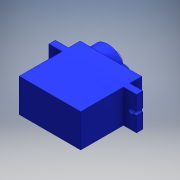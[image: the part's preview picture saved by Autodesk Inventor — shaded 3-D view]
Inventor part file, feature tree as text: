
AUTODESK INVENTOR PART (.ipt)
format: ipt  version: 2016 (Build 200138000, 138)  size: 201,216 bytes
history: native  units: mm
features: extrude x8, sketch x8
ambient origin geometry x8: Origin, YZ Plane, XZ Plane, XY Plane, X Axis, Y Axis, Z Axis, Center Point
bodies: Solid1 (feature_tree)
feature tree (16):
  extrude  "Extrusion1"  TaperAngle=0.0deg  [1 undecoded]
  extrude  "Extrusion2"  Depth=2.38mm
  extrude  "Extrusion3"  Depth=4.82mm
  extrude  "Extrusion4"  TaperAngle=0.0deg  [1 undecoded]
  extrude  "Extrusion5"  Depth=1.2mm
  extrude  "Extrusion6"  Depth=6.125mm
  extrude  "Extrusion7"  Depth=2.94mm
  extrude  "Extrusion8"  Depth=1.2mm
  sketch  "Sketch1"  dims[d3=0.0mm d7=0.0mm]
  sketch  "Sketch2"  dims[d8=4.34mm d9=2.38mm]
  sketch  "Sketch3"  dims[d10=4.82mm d11=0.0mm d12=5.44mm]
  sketch  "Sketch4"  dims[d13=4.1mm d14=0.0mm d17=0.0mm]
  sketch  "Sketch5"  dims[d19=1.2mm d20=1.2mm]
  sketch  "Sketch6"  dims[d21=0.6mm d22=6.125mm]
  sketch  "Sketch7"  dims[d24=2.94mm d25=0.0mm d27=2.13mm]
  sketch  "Sketch8"  dims[d29=6.125mm d31=1.2mm d32=1.2mm d33=0.6mm d34=2.94mm d35=0.0mm d36=1.0mm d37=6.125mm d38=5.0mm d39=2.0mm d40=0.0mm]
note: 2 required parameter values undecoded (feature->parameter linkage not recoverable at this tier; creation-order binding heuristic only, values carry confidence <= 0.55)
